# Revit family: Pedestal-WashBasinHalfPedestal-Vitra_S20Series_5281
name_source: partatom
category: Plumbing Fixtures
revit_build: Autodesk Revit 2017 (Build: 20160225_1515(x64)
units: mm (PartAtom-declared; Revit-internal decimal feet)

## family parameters
Cut with Voids When Loaded = No
Host = Face
OmniClass Number = 23.45.05.14.14
OmniClass Title = Sinks/Lavatories
Part Type = Normal
Room Calculation Point = No
Round Connector Dimension = Use Diameter
Shared = Yes

## types (1)
- Pedestal-WashBasinHalfPedestal-Vitra_S20Series_5281L003-7201
    Article No. (default) = 5281L003-7201
    BIMobject category = Sanitary - Basins
    Brand = VitrA
    CW Connection = No
    Color = White
    Default Elevation = 850 mm  [stored 2.78871 ft]
    Description = VitrA S20  Wash Basin Half Pedestal
    Design country = Turkey
    HW Connection = No
    IFC Classification = Sanitary Terminal
    Main Material = Ceramic
    Manufacturer = VitrA
    Manufacturer name = VitrA
    Model = 5281L003-7201
    Mounting type = Wall-Hung
    NBS Referans Code = 35-79-64
    NBS Referans Description = Pedestal Wash Basins
    Nominal Depth (mm) = 295 mm  [stored 0.967848 ft]
    Nominal Height (mm) = 325 mm
    Nominal Width (mm) = 185 mm
    OmniClass Code = 23.45.05.14.14
    OmniClass Description = Sinks/Lavatories
    Primary Material = White
    Product SKU = 5281L003-7201
    Product certification = https://www.vitraglobal.com
    Product data url = https://www.bimobject.com
    Product family = Wall  Mounted Half Pedestal
    Product group = S20
    Product url = https://www.vitra-bad.de
    Technical description = https://cdn.vitra.com.tr
    URL = https://vitraglobal.com
    Uniclass 1.4 Code = L7212
    Uniclass 1.4 Description = Washbasins
    Uniclass 2.0 Code = PR-35-79-64
    Uniclass 2.0 Description = Pedestal Wash Basins
    Uniclass 2015 Code = Pr_40_20_96_63
    Uniclass 2015 Name = Pedestal wash basins
    Uniformat II Code = D2010
    Uniformat II Description = Plumbing Fixtures
    Vent Connection = No
    Warranty Period (Year) = 10 Years
    Waste Connection = No
    Weight Net (kg) = 8.5
    Youtube = https://www.youtube.com

note: [stored X ft] marks values corroborated as IEEE doubles in the binary element streams (Revit-internal decimal feet)

## geometry (parser evidence)
native form markers: Sweep x3
no freeform markers — native parametric forms only
